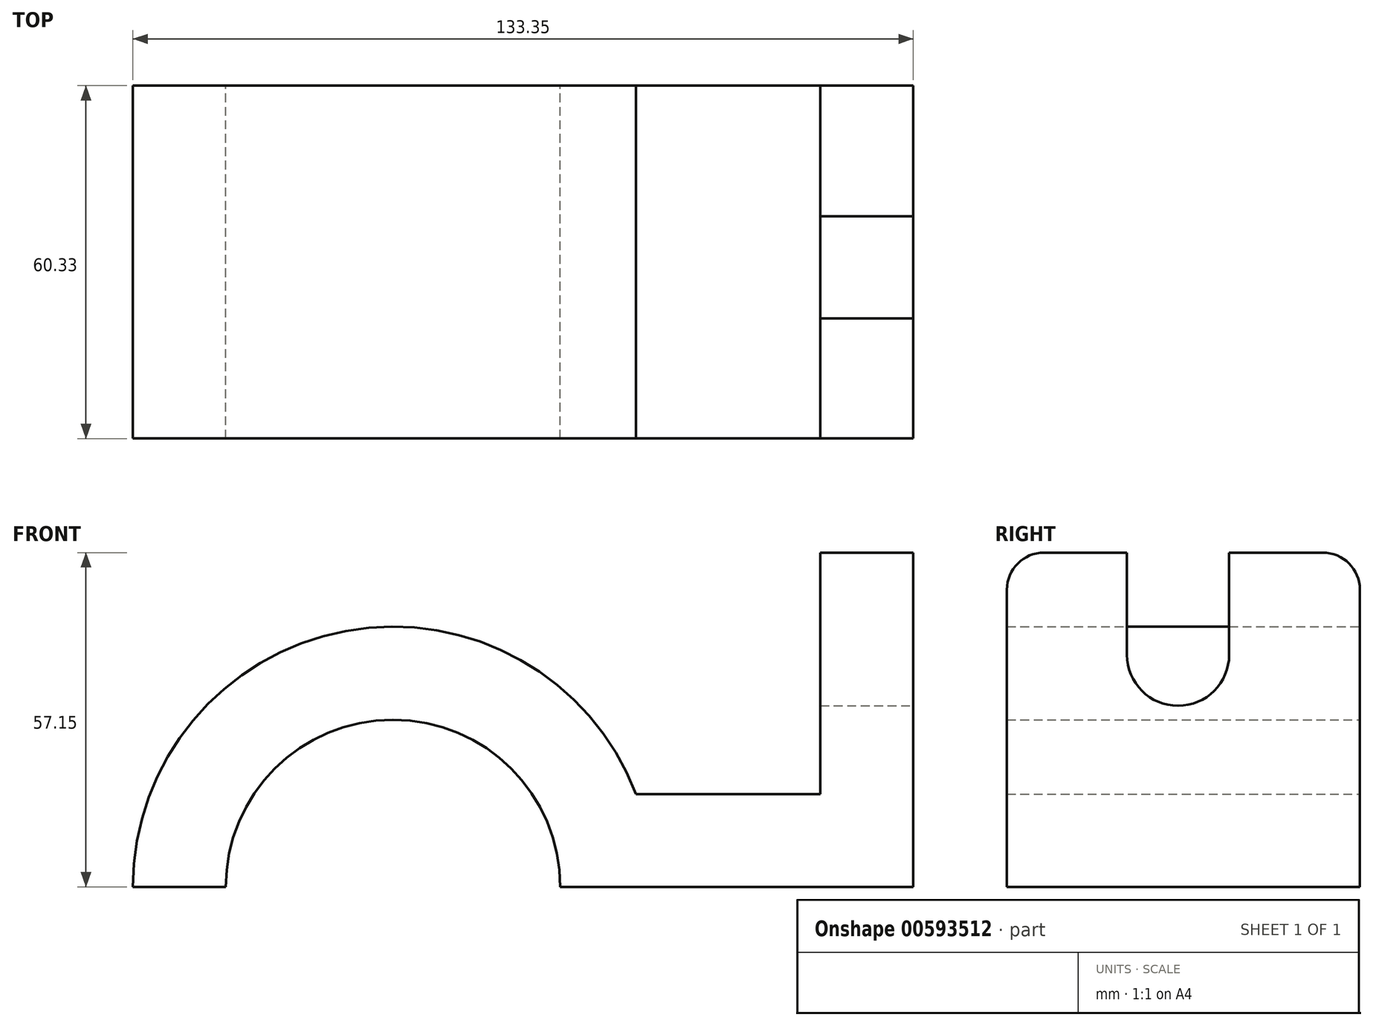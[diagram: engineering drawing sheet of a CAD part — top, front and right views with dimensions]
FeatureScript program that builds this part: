
annotation { "Feature Type Name" : "Feature", "Feature Type Description" : "" }
export const myFeature = defineFeature(function(context is Context, id is Id, definition is map)
    precondition{}
    {
        {
            var Q0;
            Q0=qCreatedBy(makeId("Front.planeOp"),FACE);
            var sketch = newSketch(context, id + "F0", { "sketchPlane" : qUnion([Q0])});
            skLineSegment(sketch, "E0", {"start": v(-67.56, 0) * mm, "end": v(-51.68, 0) * mm});
            skLineSegment(sketch, "E1", {"start": v(5.47, 0) * mm, "end": v(65.8, 0) * mm});
            skLineSegment(sketch, "E2", {"start": v(65.8, 0) * mm, "end": v(65.8, 57.15) * mm});
            skLineSegment(sketch, "E3", {"start": v(65.8, 57.15) * mm, "end": v(49.92, 57.15) * mm});
            skLineSegment(sketch, "E4", {"start": v(49.92, 57.15) * mm, "end": v(49.92, 15.88) * mm});
            skArc(sketch, "E5", {"start": v(5.47, 0) * mm, "mid": v(-23.1, 28.58) * mm, "end": v(-51.68, 0) * mm});
            skLineSegment(sketch, "E6", {"start": v(49.92, 15.88) * mm, "end": v(18.42, 15.88) * mm});
            skArc(sketch, "E7", {"start": v(18.42, 15.87) * mm, "mid": v(-31.18, 43.74) * mm, "end": v(-67.56, 0) * mm});
            skSolve(sketch);
        }
        {
            var Q0;
            Q0=makeQuery(id+"F0.imprint","IMPRINT",FACE,{"disambiguationData":[TD([[makeQuery(id+"F0.imprint","IMPRINT",EDGE,{"derivedFrom":sQuery(id+"F0.wireOp",EDGE,"E0")}),1.0]])]});
            extrude(context, id + "F1", {"entities" : qUnion([Q0]), "depth" : 60.32 * mm, "offsetDistance" : 25.4 * mm});
        }
        {
            var Q0;
            Q0=makeQuery(id+"F1.opExtrude","CAP_EDGE",EDGE,{"disambiguationData":[OSD([sQuery(id+"F0.wireOp",EDGE,"E3")])],"isStart":false});
            fillet(context, id + "F2", {"entities" : qUnion([Q0]), "radius" : 6.35 * mm, "tangentPropagation" : true, "allowEdgeOverflow" : false});
        }
        {
            var Q0;
            Q0=makeQuery(id+"F1.opExtrude","CAP_EDGE",EDGE,{"disambiguationData":[OSD([sQuery(id+"F0.wireOp",EDGE,"E3")])],"isStart":true});
            fillet(context, id + "F3", {"entities" : qUnion([Q0]), "radius" : 6.35 * mm, "tangentPropagation" : true, "allowEdgeOverflow" : false});
        }
        {
            var Q0;
            Q0=makeQuery(id+"F1.opExtrude","SWEPT_FACE",FACE,{"disambiguationData":[OSD([sQuery(id+"F0.wireOp",EDGE,"E2")])]});
            var sketch = newSketch(context, id + "F4", { "sketchPlane" : qUnion([Q0])});
            skLineSegment(sketch, "E8", {"start": v(-39.81, 57.15) * mm, "end": v(-22.35, 57.15) * mm});
            skLineSegment(sketch, "E9", {"start": v(-22.35, 57.15) * mm, "end": v(-22.35, 39.69) * mm});
            skLineSegment(sketch, "E10", {"start": v(-22.35, 39.69) * mm, "end": v(-39.81, 39.69) * mm});
            skLineSegment(sketch, "E11", {"start": v(-39.81, 39.69) * mm, "end": v(-39.81, 57.15) * mm});
            skArc(sketch, "E12", {"start": v(-39.81, 39.69) * mm, "mid": v(-31.08, 30.96) * mm, "end": v(-22.35, 39.69) * mm});
            skSolve(sketch);
        }
        {
            var Q0;
            Q0=makeQuery(id+"F4.imprint","IMPRINT",FACE,{"disambiguationData":[TD([[makeQuery(id+"F4.imprint","IMPRINT",EDGE,{"derivedFrom":sQuery(id+"F4.wireOp",EDGE,"E8")}),-1.0]])]});
            var Q1;
            Q1=makeQuery(id+"F4.imprint","IMPRINT",FACE,{"disambiguationData":[TD([[makeQuery(id+"F4.imprint","IMPRINT",EDGE,{"derivedFrom":sQuery(id+"F4.wireOp",EDGE,"E10")}),1.0]])]});
            extrude(context, id + "F5", {"entities" : qUnion([Q0, Q1]), "operationType" : NewBodyOperationType.REMOVE, "oppositeDirection" : true, "depth" : 25.4 * mm, "offsetDistance" : 25.4 * mm});
        }
    });
